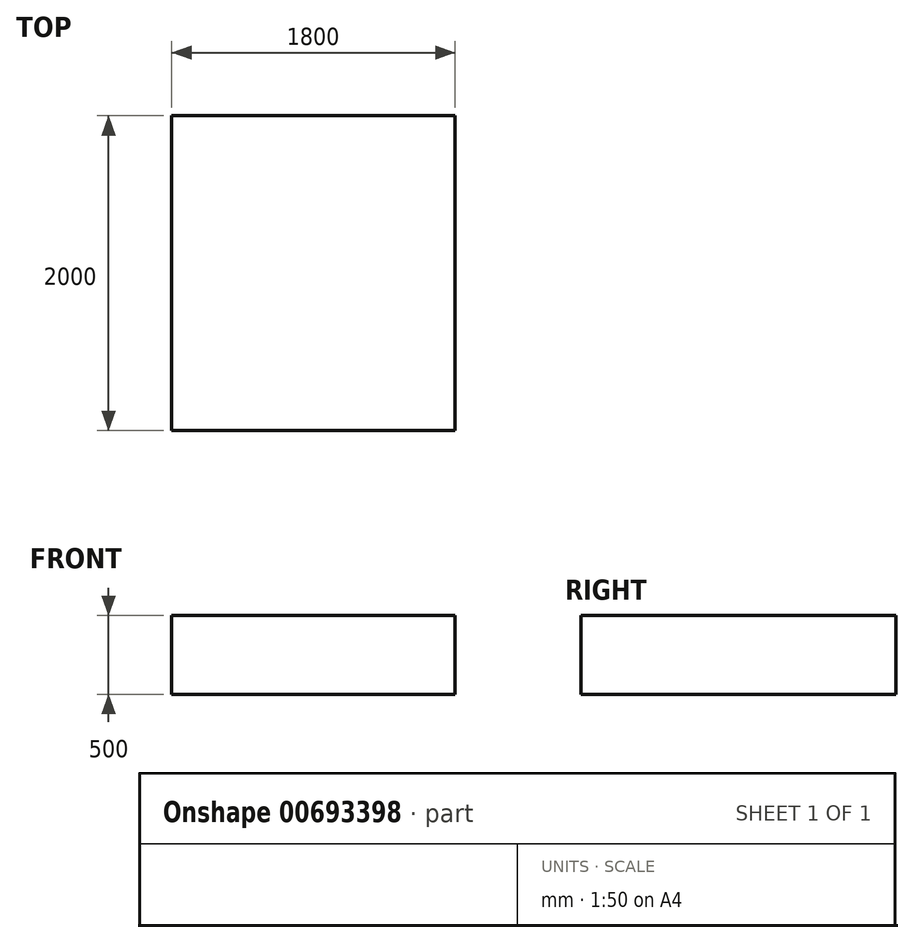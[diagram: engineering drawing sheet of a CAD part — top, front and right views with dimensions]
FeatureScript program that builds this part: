
annotation { "Feature Type Name" : "Feature", "Feature Type Description" : "" }
export const myFeature = defineFeature(function(context is Context, id is Id, definition is map)
    precondition{}
    {
        {
            var Q0;
            Q0=qCreatedBy(makeId("Top.planeOp"),FACE);
            var sketch = newSketch(context, id + "F0", { "sketchPlane" : qUnion([Q0])});
            skLineSegment(sketch, "E0.bottom", {"start": v(0, 0) * mm, "end": v(1800, 0) * mm});
            skLineSegment(sketch, "E0.top", {"start": v(0, 2000) * mm, "end": v(1800, 2000) * mm});
            skLineSegment(sketch, "E0.left", {"start": v(0, 0) * mm, "end": v(0, 2000) * mm});
            skLineSegment(sketch, "E0.right", {"start": v(1800, 0) * mm, "end": v(1800, 2000) * mm});
            skSolve(sketch);
        }
        {
            var Q0;
            Q0 = qSketchRegion(id + "F0", true);
            extrude(context, id + "F1", {"entities" : qUnion([Q0]), "depth" : 500 * mm, "offsetDistance" : 25.4 * mm});
        }
    });
